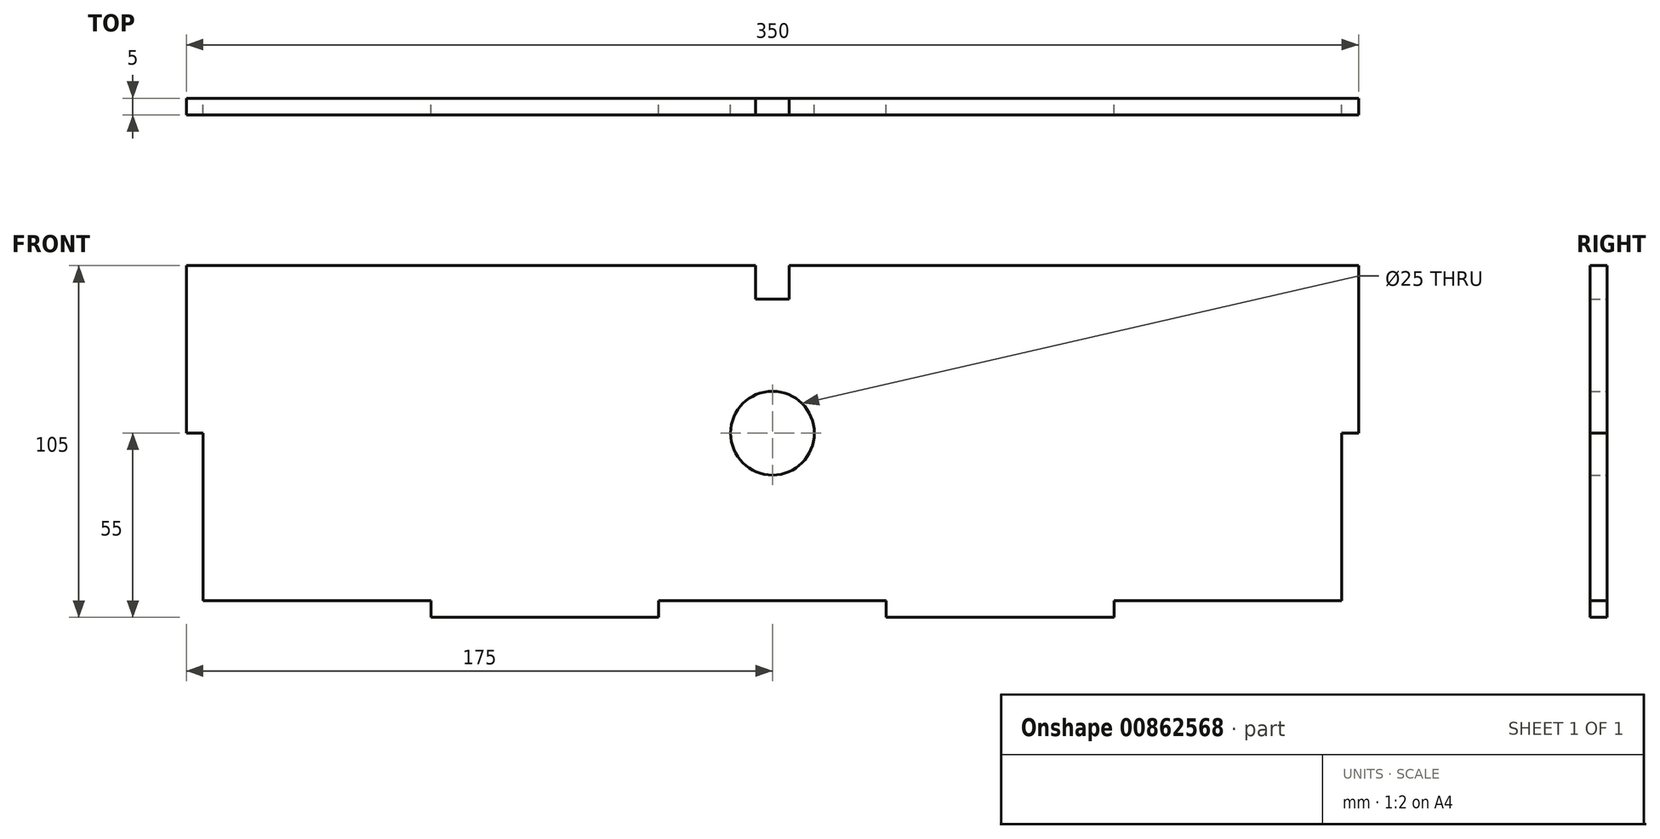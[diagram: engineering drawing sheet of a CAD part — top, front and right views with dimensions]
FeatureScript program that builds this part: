
annotation { "Feature Type Name" : "Feature", "Feature Type Description" : "" }
export const myFeature = defineFeature(function(context is Context, id is Id, definition is map)
    precondition{}
    {
        {
            var Q0;
            Q0=qCreatedBy(makeId("Front.planeOp"),FACE);
            var sketch = newSketch(context, id + "F0", { "sketchPlane" : qUnion([Q0])});
            skLineSegment(sketch, "E0.bottom", {"start": v(170, -50) * mm, "end": v(-170, -50) * mm});
            skLineSegment(sketch, "E0.top", {"start": v(170, 50) * mm, "end": v(5, 50) * mm});
            skLineSegment(sketch, "E0.left", {"start": v(170, -50) * mm, "end": v(170, 50) * mm});
            skLineSegment(sketch, "E0.right", {"start": v(-170, -50) * mm, "end": v(-170, 50) * mm});
            skPoint(sketch, "E0.middle", {"position": v(0, 0) * mm});
            skLineSegment(sketch, "E1", {"start": v(-102, -50) * mm, "end": v(-102, -55) * mm});
            skLineSegment(sketch, "E2", {"start": v(-102, -55) * mm, "end": v(-34, -55) * mm});
            skLineSegment(sketch, "E3", {"start": v(-34, -55) * mm, "end": v(-34, -50) * mm});
            skLineSegment(sketch, "E4", {"start": v(0, 80.34) * mm, "end": v(0, -109.87) * mm});
            skPoint(sketch, "E4.endSnap0", {"position": v(0, -50) * mm});
            skLineSegment(sketch, "E5.MirrorCS", {"start": v(102, -50) * mm, "end": v(102, -55) * mm});
            skLineSegment(sketch, "E6.MirrorCS", {"start": v(102, -55) * mm, "end": v(34, -55) * mm});
            skLineSegment(sketch, "E7.MirrorCS", {"start": v(34, -55) * mm, "end": v(34, -50) * mm});
            skLineSegment(sketch, "E8", {"start": v(-170, 50) * mm, "end": v(-175, 50) * mm});
            skLineSegment(sketch, "E9", {"start": v(-175, 50) * mm, "end": v(-175, 0) * mm});
            skLineSegment(sketch, "E10", {"start": v(-175, 0) * mm, "end": v(-170, 0) * mm});
            skLineSegment(sketch, "E11.MirrorCS", {"start": v(170, 50) * mm, "end": v(175, 50) * mm});
            skLineSegment(sketch, "E12.MirrorCS", {"start": v(175, 50) * mm, "end": v(175, 0) * mm});
            skLineSegment(sketch, "E13.MirrorCS", {"start": v(175, 0) * mm, "end": v(170, 0) * mm});
            skCircle(sketch, "E14", {"center": v(0, 0) * mm, "radius": 12.5 * mm});
            skLineSegment(sketch, "E15", {"start": v(-5, 50) * mm, "end": v(-5, 40) * mm});
            skLineSegment(sketch, "E16", {"start": v(-5, 40) * mm, "end": v(0, 40) * mm});
            skLineSegment(sketch, "E17.MirrorCS", {"start": v(5, 50) * mm, "end": v(5, 40) * mm});
            skLineSegment(sketch, "E18.MirrorCS", {"start": v(5, 40) * mm, "end": v(0, 40) * mm});
            skLineSegment(sketch, "E19.trimOffspring", {"start": v(-5, 50) * mm, "end": v(-170, 50) * mm});
            skSolve(sketch);
        }
        {
            var Q0;
            Q0 = qSketchRegion(id + "F0", true);
            extrude(context, id + "F1", {"entities" : qUnion([Q0]), "depth" : 5 * mm, "offsetDistance" : 25 * mm});
        }
    });
